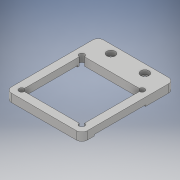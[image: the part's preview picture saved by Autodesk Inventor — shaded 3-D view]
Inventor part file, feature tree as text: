
AUTODESK INVENTOR PART (.ipt)
format: ipt  version: 2017 (Build 210142000, 142)  size: 164,864 bytes
history: native  units: mm
features: sketch x2, extrude x2, fillet x2, hole x1
ambient origin geometry x8: Origin, YZ Plane, XZ Plane, XY Plane, X Axis, Y Axis, Z Axis, Center Point
bodies: Solid1 (feature_tree)
feature tree (7):
  sketch  "Sketch1"  dims[d0=22.2mm d1=22.2mm]
  extrude  "Extrusion1"  Depth=22.2mm
  hole  "Hole1"  [1 undecoded]
  fillet  "Fillet1"  Radius=6.0mm
  fillet  "Fillet2"  Radius=12.5mm
  extrude  "Extrusion2"  Depth=2.0mm
  sketch  "Sketch2"  dims[d2=28.0mm d3=28.0mm d4=6.0mm d5=12.5mm d6=2.0mm d7=20.0mm d9=22.2mm d10=20.0mm d12=22.2mm d15=3.0mm d16=0.0mm d17=3.0mm d18=3.1mm d19=6.0mm d20=6.0mm d21=2.0mm d22=90.0deg d23=8.0mm d24=20.594885mm d25=2.0mm d26=2.0mm d27=19.0mm d28=0.5mm d29=0.0mm]
note: 1 required parameter value undecoded (feature->parameter linkage not recoverable at this tier; creation-order binding heuristic only, values carry confidence <= 0.55)
